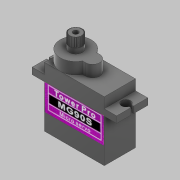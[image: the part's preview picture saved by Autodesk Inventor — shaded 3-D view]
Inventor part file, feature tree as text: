
AUTODESK INVENTOR PART (.ipt)
format: ipt  version: 2022.2 (Build 262287010, 287A)  size: 439,296 bytes
history: native  units: mm
features: sketch x11, extrude x9, other x5, pattern_circular x1, projected_geometry x1
ambient origin geometry x8: Origin, YZ Plane, XZ Plane, XY Plane, X Axis, Y Axis, Z Axis, Center Point
bodies: Body1 (feature_tree)
feature tree (27):
  other  "Sólido1"
  extrude  "Extrusión1"  Depth=12.0mm
  extrude  "Extrusión2"  Depth=5.5mm
  extrude  "Extrusión3"  Depth=4.5mm
  extrude  "Extrusión4"  Depth=3.5mm TaperAngle=0.0deg
  pattern_circular  "Patrón circular1"  [2 undecoded]
  extrude  "Extrusión5"  Depth=6.0mm
  extrude  "Extrusión6"  Depth=6.0mm
  extrude  "Extrusión7"  Depth=1.0mm
  extrude  "Extrusión8"  Depth=1.0mm
  extrude  "Extrusión9"  Depth=3.5mm
  other  "Calcomanía1"
  other  "Calcomanía2"
  sketch  "Boceto1"  dims[d0=23.0mm d1=12.0mm]
  sketch  "Boceto2"  dims[d2=23.0mm d3=0.0mm d4=5.5mm d5=6.5mm]
  sketch  "Boceto3"  dims[d6=4.5mm d7=0.0mm d8=5.0mm]
  sketch  "Boceto4"  dims[d9=5.5mm d10=0.0mm d11=3.5mm d12=0.0mm]
  sketch  "Boceto5"  dims[d13=685.0mm d14=360.0deg]
  projected_geometry  "Contorno proyectado1"
  sketch  "Boceto6"  dims[d16=2.0mm]
  sketch  "Boceto7"  dims[d17=2.0mm d18=0.0mm]
  sketch  "Boceto8"  dims[d19=16.5mm]
  sketch  "Boceto9"  dims[d20=2.5mm]
  sketch  "Boceto10"  dims[d21=4.75mm d22=0.0mm]
  other  "Imagen1"
  sketch  "Boceto11"  dims[d23=2.5mm d24=4.75mm d25=0.0mm d26=6.0mm d27=6.0mm d28=2.375mm d29=2.375mm d30=3.5mm d31=3.5mm d32=4.75mm d33=0.0mm d34=5.5mm d35=5.5mm d36=1.0mm d37=1.0mm d38=0.0mm d39=0.0mm]
  other  "Imagen2"
note: 2 required parameter values undecoded (feature->parameter linkage not recoverable at this tier; creation-order binding heuristic only, values carry confidence <= 0.55)
